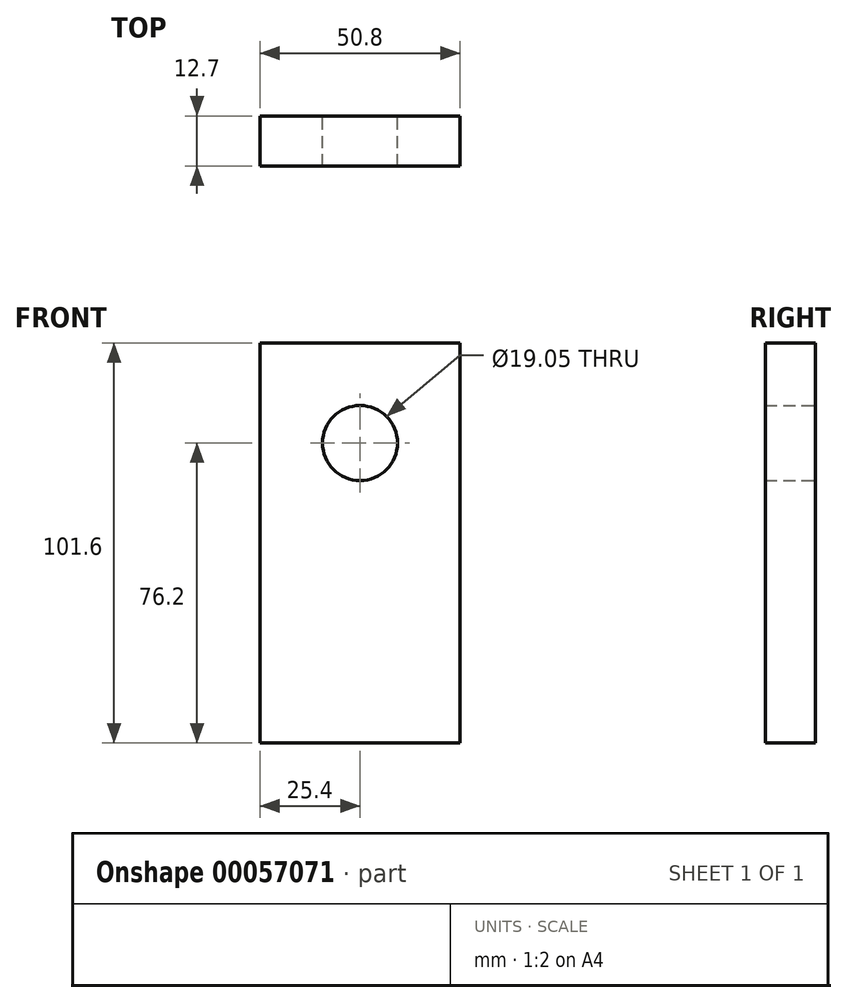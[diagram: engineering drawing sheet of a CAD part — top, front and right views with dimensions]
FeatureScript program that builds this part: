
annotation { "Feature Type Name" : "Feature", "Feature Type Description" : "" }
export const myFeature = defineFeature(function(context is Context, id is Id, definition is map)
    precondition{}
    {
        {
            var Q0;
            Q0=qCreatedBy(makeId("Front.planeOp"),FACE);
            var sketch = newSketch(context, id + "F0", { "sketchPlane" : qUnion([Q0])});
            skLineSegment(sketch, "E0.rect.bottom", {"start": v(-25.4, 50.8) * mm, "end": v(25.4, 50.8) * mm});
            skLineSegment(sketch, "E0.rect.top", {"start": v(-25.4, -50.8) * mm, "end": v(25.4, -50.8) * mm});
            skLineSegment(sketch, "E0.rect.left", {"start": v(-25.4, 50.8) * mm, "end": v(-25.4, -50.8) * mm});
            skLineSegment(sketch, "E0.rect.right", {"start": v(25.4, 50.8) * mm, "end": v(25.4, -50.8) * mm});
            skPoint(sketch, "E0.rect.middle", {"position": v(0, 0) * mm});
            skCircle(sketch, "E1", {"center": v(0, 25.4) * mm, "radius": 9.53 * mm});
            skSolve(sketch);
        }
        {
            var Q0;
            Q0=makeQuery(id+"F0.imprint","IMPRINT",FACE,{"disambiguationData":[TD([[makeQuery(id+"F0.imprint","IMPRINT",EDGE,{"derivedFrom":sQuery(id+"F0.wireOp",EDGE,"E0.rect.bottom")}),-1.0]])]});
            extrude(context, id + "F1", {"entities" : qUnion([Q0]), "depth" : 12.7 * mm});
        }
    });
